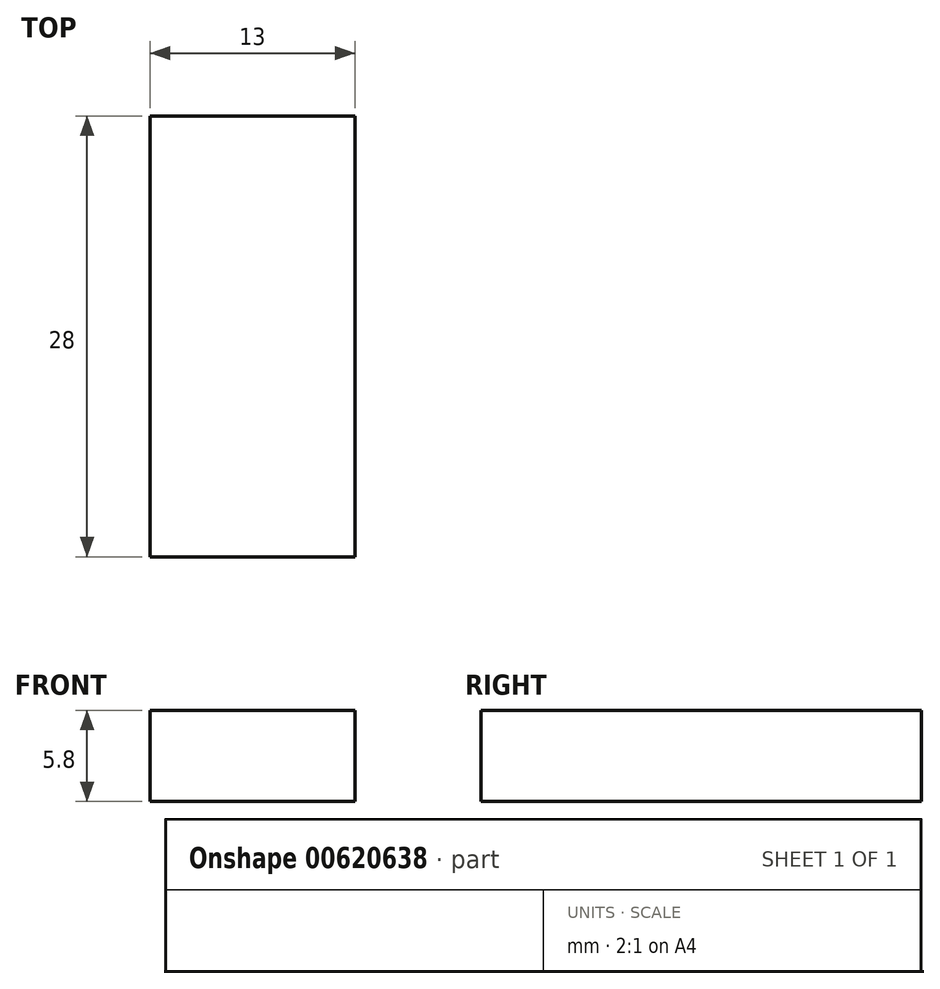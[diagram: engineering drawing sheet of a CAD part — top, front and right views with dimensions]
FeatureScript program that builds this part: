
annotation { "Feature Type Name" : "Feature", "Feature Type Description" : "" }
export const myFeature = defineFeature(function(context is Context, id is Id, definition is map)
    precondition{}
    {
        {
            var Q0;
            Q0=qCreatedBy(makeId("Top.planeOp"),FACE);
            var sketch = newSketch(context, id + "F0", { "sketchPlane" : qUnion([Q0])});
            skLineSegment(sketch, "E0.bottom", {"start": v(-6.5, 14) * mm, "end": v(6.5, 14) * mm});
            skLineSegment(sketch, "E0.top", {"start": v(-6.5, -14) * mm, "end": v(6.5, -14) * mm});
            skLineSegment(sketch, "E0.left", {"start": v(-6.5, 14) * mm, "end": v(-6.5, -14) * mm});
            skLineSegment(sketch, "E0.right", {"start": v(6.5, 14) * mm, "end": v(6.5, -14) * mm});
            skPoint(sketch, "E0.middle", {"position": v(0, 0) * mm});
            skSolve(sketch);
        }
        {
            var Q0;
            Q0=makeQuery(id+"F0.imprint","IMPRINT",FACE,{"disambiguationData":[TD([[makeQuery(id+"F0.imprint","IMPRINT",EDGE,{"derivedFrom":sQuery(id+"F0.wireOp",EDGE,"E0.bottom")}),-1.0]])]});
            extrude(context, id + "F1", {"entities" : qUnion([Q0]), "depth" : 5.8 * mm, "offsetDistance" : 25 * mm});
        }
    });
